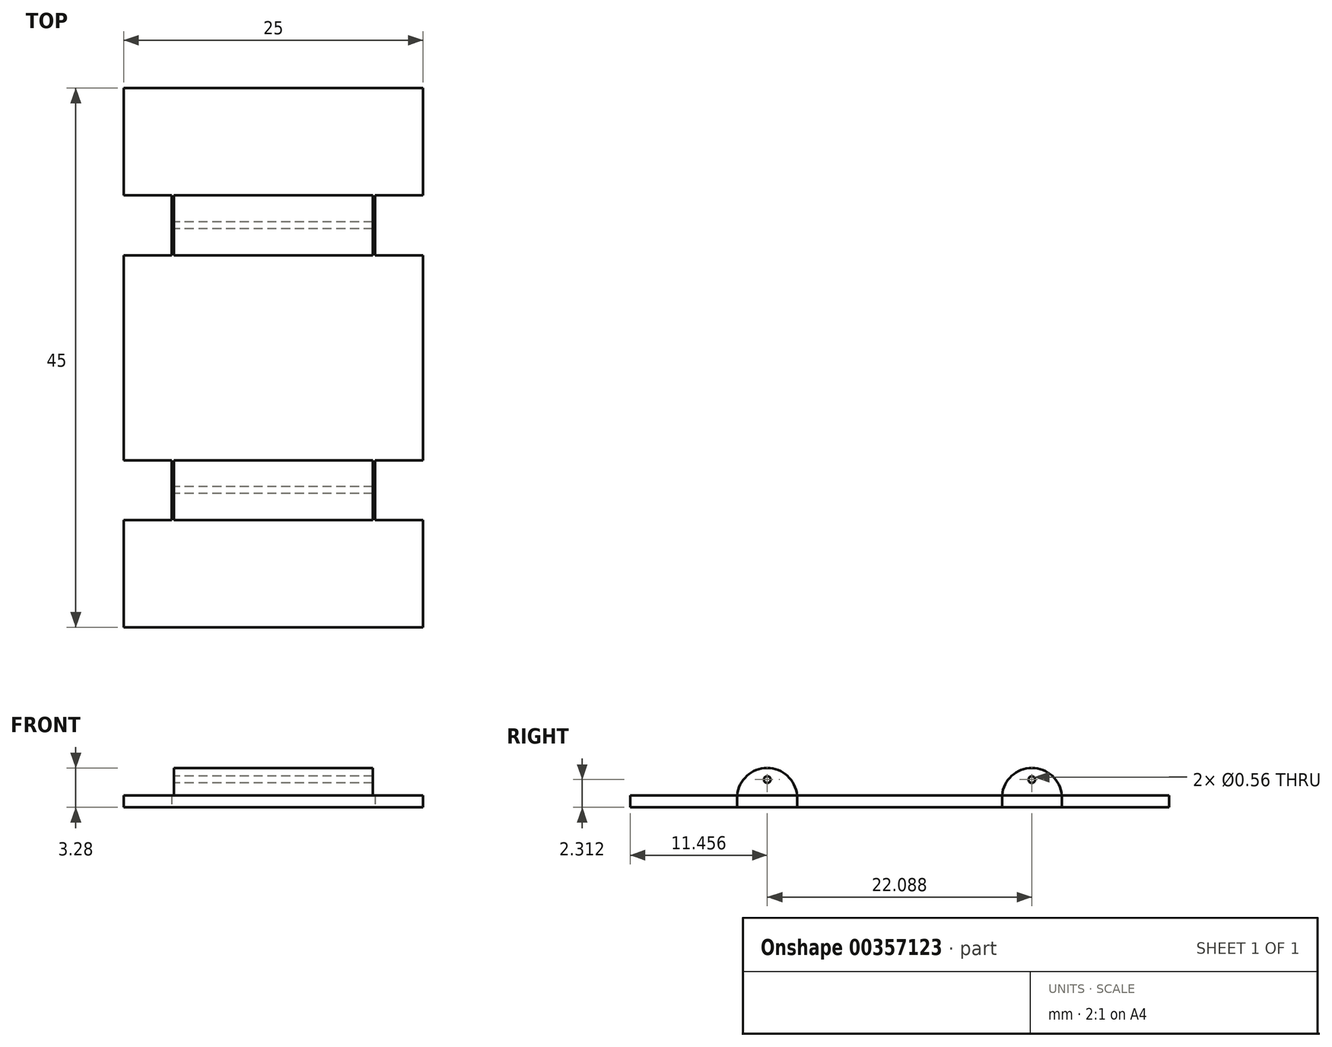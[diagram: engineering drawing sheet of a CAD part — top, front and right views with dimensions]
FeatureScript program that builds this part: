
annotation { "Feature Type Name" : "Feature", "Feature Type Description" : "" }
export const myFeature = defineFeature(function(context is Context, id is Id, definition is map)
    precondition{}
    {
        {
            var Q0;
            Q0=qCreatedBy(makeId("Top.planeOp"),FACE);
            var sketch = newSketch(context, id + "F0", { "sketchPlane" : qUnion([Q0])});
            skLineSegment(sketch, "E0.bottom", {"start": v(-12.5, -22.5) * mm, "end": v(12.5, -22.5) * mm});
            skLineSegment(sketch, "E0.top", {"start": v(-12.5, 22.5) * mm, "end": v(12.5, 22.5) * mm});
            skLineSegment(sketch, "E0.left", {"start": v(-12.5, -22.5) * mm, "end": v(-12.5, 22.5) * mm});
            skLineSegment(sketch, "E0.right", {"start": v(12.5, -22.5) * mm, "end": v(12.5, 22.5) * mm});
            skPoint(sketch, "E0.middle", {"position": v(0, 0) * mm});
            skLineSegment(sketch, "E1.bottom", {"start": v(-12.5, 13.55) * mm, "end": v(-8.5, 13.55) * mm});
            skLineSegment(sketch, "E1.top", {"start": v(-12.5, 8.55) * mm, "end": v(-8.5, 8.55) * mm});
            skLineSegment(sketch, "E1.left", {"start": v(-12.5, 13.55) * mm, "end": v(-12.5, 8.55) * mm});
            skLineSegment(sketch, "E1.right", {"start": v(-8.5, 13.55) * mm, "end": v(-8.5, 8.55) * mm});
            skPoint(sketch, "E1.middle", {"position": v(-10.5, 11.05) * mm});
            skLineSegment(sketch, "E2.MirrorCS", {"start": v(8.5, 13.55) * mm, "end": v(8.5, 8.55) * mm});
            skLineSegment(sketch, "E3.MirrorCS", {"start": v(12.5, 8.55) * mm, "end": v(8.5, 8.55) * mm});
            skLineSegment(sketch, "E4.MirrorCS", {"start": v(12.5, 13.55) * mm, "end": v(8.5, 13.55) * mm});
            skLineSegment(sketch, "E5.MirrorCS", {"start": v(-12.5, -8.55) * mm, "end": v(-8.5, -8.55) * mm});
            skLineSegment(sketch, "E6.MirrorCS", {"start": v(-12.5, -13.55) * mm, "end": v(-8.5, -13.55) * mm});
            skLineSegment(sketch, "E7.MirrorCS", {"start": v(-8.5, -13.55) * mm, "end": v(-8.5, -8.55) * mm});
            skLineSegment(sketch, "E8.MirrorCS", {"start": v(12.5, -8.55) * mm, "end": v(8.5, -8.55) * mm});
            skLineSegment(sketch, "E9.MirrorCS", {"start": v(12.5, -13.55) * mm, "end": v(8.5, -13.55) * mm});
            skLineSegment(sketch, "E10.MirrorCS", {"start": v(8.5, -13.55) * mm, "end": v(8.5, -8.55) * mm});
            skSolve(sketch);
        }
        {
            var Q0;
            {var subQ5=sQuery(id+"F0.wireOp",EDGE,"E0.bottom");Q0=makeQuery(id+"F0.imprint","IMPRINT",FACE,{"disambiguationData":[TD([[makeQuery(id+"F0.imprint","IMPRINT",EDGE,{"derivedFrom":subQ5}),1.0]])]});}
            extrude(context, id + "F1", {"entities" : qUnion([Q0]), "depth" : 1 * mm});
        }
        {
            var Q0;
            Q0=qCreatedBy(makeId("Right.planeOp"),FACE);
            var sketch = newSketch(context, id + "F2", { "sketchPlane" : qUnion([Q0])});
            skArc(sketch, "E11", {"start": v(-8.56, 1) * mm, "mid": v(-11.05, 3.28) * mm, "end": v(-13.55, 1) * mm});
            skCircle(sketch, "E12", {"center": v(-11.04, 2.31) * mm, "radius": 0.28 * mm});
            skArc(sketch, "E13.MirrorCS", {"start": v(8.56, 1) * mm, "mid": v(11.05, 3.28) * mm, "end": v(13.55, 1) * mm});
            skCircle(sketch, "E14.MirrorC", {"center": v(11.04, 2.31) * mm, "radius": 0.28 * mm});
            skLineSegment(sketch, "E15", {"start": v(-13.55, 1) * mm, "end": v(-8.56, 1) * mm});
            skLineSegment(sketch, "E16", {"start": v(8.56, 1) * mm, "end": v(13.55, 1) * mm});
            skSolve(sketch);
        }
        {
            var Q0;
            Q0 = qSketchRegion(id + "F2", true);
            extrude(context, id + "F3", {"entities" : qUnion([Q0]), "operationType" : NewBodyOperationType.ADD, "endBound" : BoundingType.SYMMETRIC, "depth" : 16.6 * mm});
        }
    });
